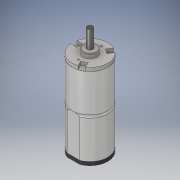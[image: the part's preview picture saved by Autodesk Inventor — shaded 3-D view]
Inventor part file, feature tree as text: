
AUTODESK INVENTOR PART (.ipt)
format: ipt  version: 2019 (Build 230136000, 136)  size: 295,424 bytes
history: native  units: in
note: dims shown in document units (in); Inventor stores cm internally (conversion verified against a paired STEP export)
features: sketch x13, extrude x12, fillet x2, plane x2, hole x1
ambient origin geometry x8: Origin, YZ Plane, XZ Plane, XY Plane, X Axis, Y Axis, Z Axis, Center Point
bodies: Solid1 (feature_tree)
feature tree (30):
  extrude  "Extrusion1"  Depth=0.75in TaperAngle=0.0deg
  fillet  "Fillet1"  Radius=0.025in
  extrude  "Extrusion2"  Depth=0.025in
  fillet  "Fillet2"  Radius=0.75in
  extrude  "Extrusion3"  Depth=0.1761in
  extrude  "Extrusion4"  Depth=0.2825in
  extrude  "Extrusion5"  Depth=0.1875in
  extrude  "Extrusion6"  Depth=0.0417in TaperAngle=0.0deg
  extrude  "Extrusion7"  Depth=0.0625in TaperAngle=0.0deg
  extrude  "Extrusion8"  Depth=0.0156in TaperAngle=0.0deg
  plane  "Work Plane1"
  extrude  "Extrusion9"  [1 undecoded]
  hole  "Hole1"  [1 undecoded]
  extrude  "Extrusion10"  Depth=0.2188in
  extrude  "Extrusion11"  Depth=0.2188in
  plane  "Work Plane2"
  extrude  "Extrusion12"  Depth=0.1in
  sketch  "Sketch1"  dims[d0=0.625in d1=0.75in d2=0.0in d3=0.025in]
  sketch  "Sketch2"  dims[d4=0.75in d5=0.0in d6=0.025in d10=0.75in d11=0.0in]
  sketch  "Sketch3"  dims[d12=0.2248in d13=0.1761in]
  sketch  "Sketch4"  dims[d14=0.2825in d15=0.2248in]
  sketch  "Sketch5"  dims[d16=0.0208in d17=0.0in d18=0.1875in]
  sketch  "Sketch6"  dims[d19=0.0625in d20=0.0417in d21=0.0in]
  sketch  "Sketch7"  dims[d22=0.25in d23=0.0625in d24=0.0in]
  sketch  "Sketch8"  dims[d25=0.225in d26=0.0156in d27=0.0in]
  sketch  "Sketch9"  dims[d28=0.0312in d29=0.0in d30=-0.0625in]
  sketch  "Sketch10"  dims[d31=0.62in d32=0.001in d33=0.0in d34=0.003in]
  sketch  "Sketch11"  dims[d35=0.003in d38=0.2188in]
  sketch  "Sketch13"  dims[d39=0.1094in d40=0.2188in]
  sketch  "Sketch14"  dims[d41=0.1094in d42=0.0312in d43=0.75in d44=0.375in d45=0.25in d46=0.5635in d47=0.25in d48=0.0in d49=0.1in d50=0.3125in d51=0.0in d55=0.1in d56=90.0deg d57=0.0878in d58=0.0572in d59=0.1327in d60=1.1811in d62=360.0deg d64=0.0625in d65=0.0in d66=-0.0625in d67=0.62in d68=0.001in d69=0.0in]
note: 2 required parameter values undecoded (feature->parameter linkage not recoverable at this tier; creation-order binding heuristic only, values carry confidence <= 0.55)
